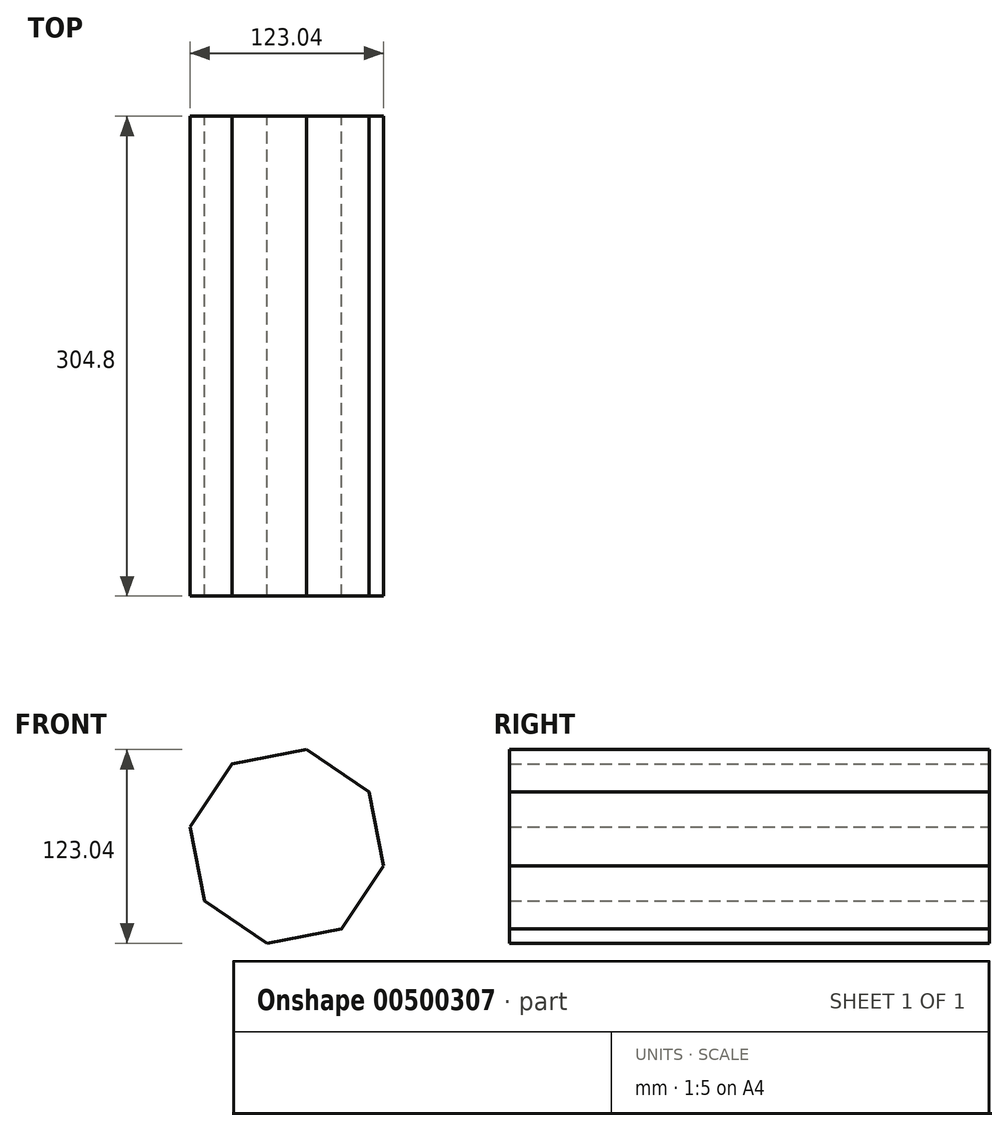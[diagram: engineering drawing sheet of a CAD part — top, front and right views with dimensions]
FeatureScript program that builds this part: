
annotation { "Feature Type Name" : "Feature", "Feature Type Description" : "" }
export const myFeature = defineFeature(function(context is Context, id is Id, definition is map)
    precondition{}
    {
        {
            var Q0;
            Q0=qCreatedBy(makeId("Front.planeOp"),FACE);
            var sketch = newSketch(context, id + "F0", { "sketchPlane" : qUnion([Q0])});
            skCircle(sketch, "E0.cCircle", {"center": v(0, 0) * mm, "radius": 62.77 * mm, "construction": true});
            skLineSegment(sketch, "E0.0", {"start": v(-34.69, 52.32) * mm, "end": v(12.47, 61.52) * mm});
            skLineSegment(sketch, "E0.1", {"start": v(12.47, 61.52) * mm, "end": v(52.32, 34.69) * mm});
            skLineSegment(sketch, "E0.2", {"start": v(52.32, 34.69) * mm, "end": v(61.52, -12.47) * mm});
            skLineSegment(sketch, "E0.3", {"start": v(61.52, -12.47) * mm, "end": v(34.69, -52.32) * mm});
            skLineSegment(sketch, "E0.4", {"start": v(34.69, -52.32) * mm, "end": v(-12.47, -61.52) * mm});
            skLineSegment(sketch, "E0.5", {"start": v(-12.47, -61.52) * mm, "end": v(-52.32, -34.69) * mm});
            skLineSegment(sketch, "E0.6", {"start": v(-52.32, -34.69) * mm, "end": v(-61.52, 12.47) * mm});
            skLineSegment(sketch, "E0.7", {"start": v(-61.52, 12.47) * mm, "end": v(-34.69, 52.32) * mm});
            skSolve(sketch);
        }
        {
            var Q0;
            Q0=makeQuery(id+"F0.imprint","IMPRINT",FACE,{"disambiguationData":[TD([[makeQuery(id+"F0.imprint","IMPRINT",EDGE,{"derivedFrom":sQuery(id+"F0.wireOp",EDGE,"E0.0")}),-1.0]])]});
            extrude(context, id + "F1", {"entities" : qUnion([Q0]), "depth" : 304.8 * mm});
        }
    });
